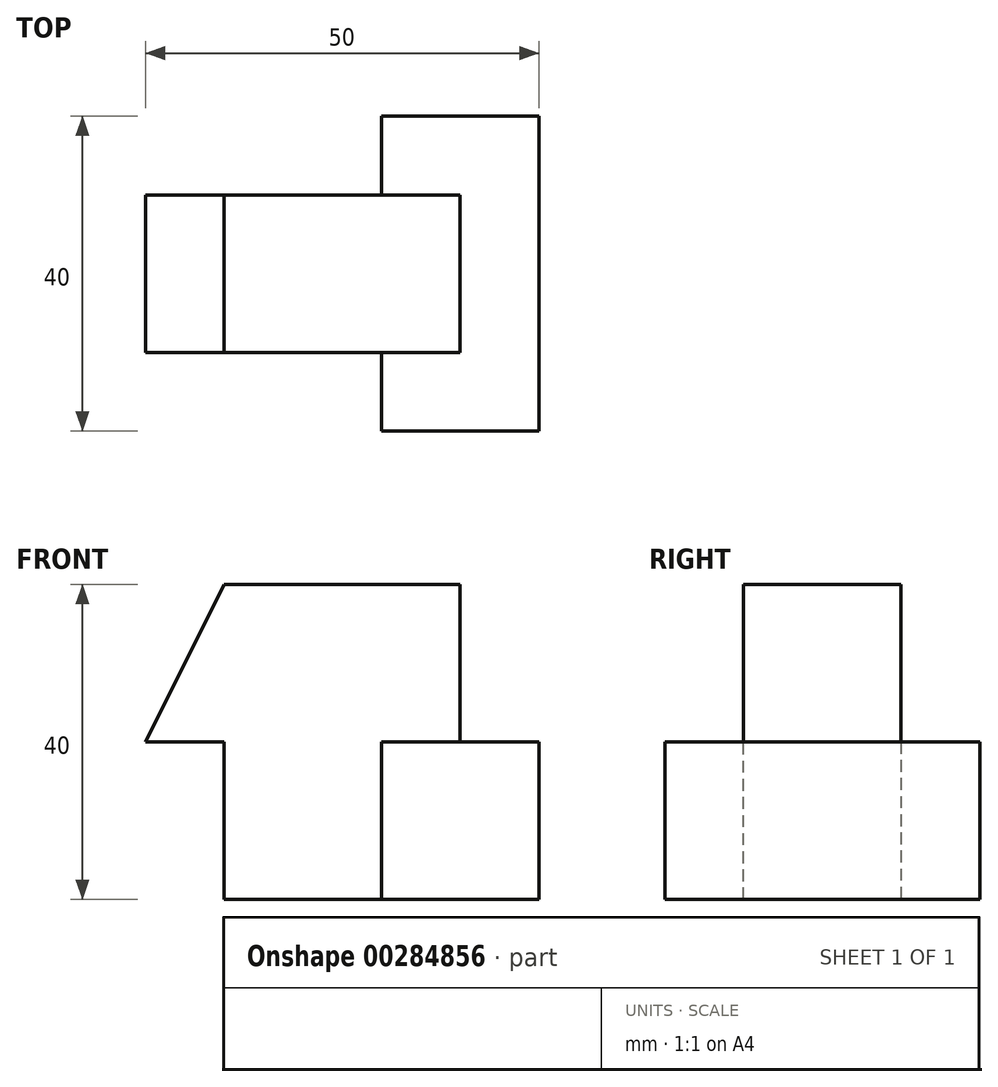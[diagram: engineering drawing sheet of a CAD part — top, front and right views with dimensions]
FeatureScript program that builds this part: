
annotation { "Feature Type Name" : "Feature", "Feature Type Description" : "" }
export const myFeature = defineFeature(function(context is Context, id is Id, definition is map)
    precondition{}
    {
        {
            var Q0;
            Q0=qCreatedBy(makeId("Front.planeOp"),FACE);
            var sketch = newSketch(context, id + "F0", { "sketchPlane" : qUnion([Q0])});
            skLineSegment(sketch, "E0.bottom", {"start": v(0, 0) * mm, "end": v(50, 0) * mm});
            skLineSegment(sketch, "E0.top", {"start": v(0, 40) * mm, "end": v(50, 40) * mm});
            skLineSegment(sketch, "E0.left", {"start": v(0, 0) * mm, "end": v(0, 40) * mm});
            skLineSegment(sketch, "E0.right", {"start": v(50, 0) * mm, "end": v(50, 40) * mm});
            skSolve(sketch);
        }
        {
            var Q0;
            Q0=makeQuery(id+"F0.imprint","IMPRINT",FACE,{"disambiguationData":[TD([[makeQuery(id+"F0.imprint","IMPRINT",EDGE,{"derivedFrom":sQuery(id+"F0.wireOp",EDGE,"E0.bottom")}),1.0]])]});
            extrude(context, id + "F1", {"entities" : qUnion([Q0]), "depth" : 40 * mm});
        }
        {
            var Q0;
            Q0=makeQuery(id+"F1.opExtrude","SWEPT_FACE",FACE,{"disambiguationData":[OSD([sQuery(id+"F0.wireOp",EDGE,"E0.left")])]});
            var sketch = newSketch(context, id + "F2", { "sketchPlane" : qUnion([Q0])});
            skLineSegment(sketch, "E1", {"start": v(0, 20) * mm, "end": v(40, 20) * mm});
            skLineSegment(sketch, "E2", {"start": v(30, 40) * mm, "end": v(30, 20) * mm});
            skLineSegment(sketch, "E3", {"start": v(10, 40) * mm, "end": v(10, 20) * mm});
            skLineSegment(sketch, "E4.0", {"start": v(40, 40) * mm, "end": v(0, 40) * mm});
            skLineSegment(sketch, "E5.0.1", {"start": v(40, 40) * mm, "end": v(40, 20) * mm});
            skLineSegment(sketch, "E5.0.3", {"start": v(40, 20) * mm, "end": v(40, 40) * mm});
            skLineSegment(sketch, "E6.0.1", {"start": v(0, 40) * mm, "end": v(0, 20) * mm});
            skLineSegment(sketch, "E6.0.3", {"start": v(0, 0) * mm, "end": v(0, 40) * mm});
            skPoint(sketch, "E7.orphan", {"position": v(40, 0) * mm});
            skPoint(sketch, "E8.orphan", {"position": v(0, 0) * mm});
            skSolve(sketch);
        }
        {
            var Q0;
            {var subQ3=sQuery(id+"F2.wireOp",EDGE,"E3");Q0=makeQuery(id+"F2.imprint","IMPRINT",FACE,{"disambiguationData":[TD([[makeQuery(id+"F2.imprint","IMPRINT",EDGE,{"derivedFrom":subQ3}),-1.0]])]});}
            var Q1;
            {var subQ2=sQuery(id+"F2.wireOp",EDGE,"E2");Q1=makeQuery(id+"F2.imprint","IMPRINT",FACE,{"disambiguationData":[TD([[makeQuery(id+"F2.imprint","IMPRINT",EDGE,{"derivedFrom":subQ2}),1.0]])]});}
            extrude(context, id + "F3", {"entities" : qUnion([Q0, Q1]), "operationType" : NewBodyOperationType.REMOVE, "endBound" : BoundingType.THROUGH_ALL, "oppositeDirection" : true, "depth" : 30 * mm});
        }
        {
            var Q0;
            {var subQ0=sQuery(id+"F2.wireOp",EDGE,"E1");Q0=makeQuery(id+"F3.boolean.opBoolean","COPY",FACE,{"derivedFrom":makeQuery(id+"F3.opExtrude","SWEPT_FACE",FACE,{"disambiguationData":[OSD([subQ0]),TDD([makeQuery(id+"F2.imprint","IMPRINT",EDGE,{"disambiguationData":[TD([[makeQuery(id+"F2.imprint","INTERSECT",VERTEX,{"derivedFrom":[subQ0,sQuery(id+"F2.wireOp",EDGE,"E6.0.3")]}),-1.0]])],"derivedFrom":subQ0})])]})});}
            var sketch = newSketch(context, id + "F4", { "sketchPlane" : qUnion([Q0])});
            skLineSegment(sketch, "E9.0", {"start": v(50, 0) * mm, "end": v(30, 0) * mm});
            skLineSegment(sketch, "E10.0", {"start": v(50, -10) * mm, "end": v(30, -10) * mm});
            skLineSegment(sketch, "E11.0", {"start": v(50, -30) * mm, "end": v(30, -30) * mm});
            skLineSegment(sketch, "E12.0", {"start": v(50, -40) * mm, "end": v(30, -40) * mm});
            skLineSegment(sketch, "E13", {"start": v(30, 0) * mm, "end": v(30, -10) * mm});
            skLineSegment(sketch, "E14", {"start": v(30, -30) * mm, "end": v(30, -40) * mm});
            skLineSegment(sketch, "E15.0", {"start": v(50, -30) * mm, "end": v(50, -40) * mm});
            skLineSegment(sketch, "E16.0", {"start": v(50, 0) * mm, "end": v(50, -10) * mm});
            skPoint(sketch, "E17.orphan", {"position": v(0, -10) * mm});
            skPoint(sketch, "E18.orphan", {"position": v(0, -30) * mm});
            skPoint(sketch, "E19.orphan", {"position": v(0, -40) * mm});
            skPoint(sketch, "E20.orphan", {"position": v(0, 0) * mm});
            skLineSegment(sketch, "E21.0", {"start": v(50, 0) * mm, "end": v(0, 0) * mm});
            skLineSegment(sketch, "E22.0", {"start": v(50, -10) * mm, "end": v(0, -10) * mm});
            skLineSegment(sketch, "E23.0", {"start": v(0, 0) * mm, "end": v(0, -10) * mm});
            skLineSegment(sketch, "E24.0", {"start": v(0, -30) * mm, "end": v(0, -40) * mm});
            skLineSegment(sketch, "E25.0", {"start": v(50, -40) * mm, "end": v(0, -40) * mm});
            skLineSegment(sketch, "E26.0", {"start": v(50, -30) * mm, "end": v(0, -30) * mm});
            skSolve(sketch);
        }
        {
            var Q0;
            {var subQ0=sQuery(id+"F4.wireOp",EDGE,"E13");Q0=makeQuery(id+"F4.imprint","IMPRINT",FACE,{"disambiguationData":[TD([[makeQuery(id+"F4.imprint","IMPRINT",EDGE,{"derivedFrom":subQ0}),-1.0]])]});}
            var Q1;
            {var subQ0=sQuery(id+"F4.wireOp",EDGE,"E14");Q1=makeQuery(id+"F4.imprint","IMPRINT",FACE,{"disambiguationData":[TD([[makeQuery(id+"F4.imprint","IMPRINT",EDGE,{"derivedFrom":subQ0}),-1.0]])]});}
            extrude(context, id + "F5", {"entities" : qUnion([Q0, Q1]), "operationType" : NewBodyOperationType.REMOVE, "endBound" : BoundingType.THROUGH_ALL, "oppositeDirection" : true, "depth" : 25 * mm});
        }
        {
            var Q0;
            Q0=makeQuery(id+"F1.opExtrude","SWEPT_FACE",FACE,{"disambiguationData":[OSD([sQuery(id+"F0.wireOp",EDGE,"E0.top")])]});
            var sketch = newSketch(context, id + "F6", { "sketchPlane" : qUnion([Q0])});
            skLineSegment(sketch, "E27", {"start": v(40, -10) * mm, "end": v(40, -30) * mm});
            skLineSegment(sketch, "E28.0", {"start": v(50, -10) * mm, "end": v(0, -10) * mm});
            skLineSegment(sketch, "E29.0", {"start": v(50, -30) * mm, "end": v(50, -10) * mm});
            skLineSegment(sketch, "E30.0", {"start": v(50, -30) * mm, "end": v(0, -30) * mm});
            skSolve(sketch);
        }
        {
            var Q0;
            Q0=qSketchRegion(id+"F6",true);
            var Q1;
            {var subQ0=sQuery(id+"F2.wireOp",EDGE,"E1");Q1=makeQuery(id+"F3.boolean.opBoolean","COPY",FACE,{"derivedFrom":makeQuery(id+"F3.opExtrude","SWEPT_FACE",FACE,{"disambiguationData":[OSD([subQ0]),TDD([makeQuery(id+"F2.imprint","IMPRINT",EDGE,{"disambiguationData":[TD([[makeQuery(id+"F2.imprint","INTERSECT",VERTEX,{"derivedFrom":[subQ0,sQuery(id+"F2.wireOp",EDGE,"E6.0.3")]}),-1.0]])],"derivedFrom":subQ0})])]})});}
            extrude(context, id + "F7", {"entities" : qUnion([Q0]), "operationType" : NewBodyOperationType.REMOVE, "endBound" : BoundingType.UP_TO_SURFACE, "oppositeDirection" : true, "endBoundEntityFace" : qUnion([Q1]), "depth" : 25 * mm});
        }
        {
            var Q0;
            Q0=makeQuery(id+"F5.boolean.opBoolean","MERGE",FACE,{"derivedFrom":[makeQuery(id+"F3.boolean.opBoolean","COPY",FACE,{"derivedFrom":makeQuery(id+"F3.opExtrude","SWEPT_FACE",FACE,{"disambiguationData":[OSD([sQuery(id+"F2.wireOp",EDGE,"E2")])]})}),makeQuery(id+"F5.opExtrude","SWEPT_FACE",FACE,{"disambiguationData":[OSD([sQuery(id+"F4.wireOp",EDGE,"E26.0")])]})]});
            var sketch = newSketch(context, id + "F8", { "sketchPlane" : qUnion([Q0])});
            skLineSegment(sketch, "E31.bottom", {"start": v(0, 40) * mm, "end": v(10, 40) * mm});
            skLineSegment(sketch, "E31.top", {"start": v(0, 20) * mm, "end": v(10, 20) * mm});
            skLineSegment(sketch, "E31.left", {"start": v(0, 40) * mm, "end": v(0, 20) * mm});
            skLineSegment(sketch, "E31.right", {"start": v(10, 40) * mm, "end": v(10, 20) * mm});
            skLineSegment(sketch, "E32", {"start": v(10, 40) * mm, "end": v(0, 20) * mm});
            skSolve(sketch);
        }
        {
            var Q0;
            Q0=makeQuery(id+"F8.imprint","IMPRINT",FACE,{"disambiguationData":[TD([[makeQuery(id+"F8.imprint","IMPRINT",EDGE,{"derivedFrom":sQuery(id+"F8.wireOp",EDGE,"E31.bottom")}),1.0]])]});
            extrude(context, id + "F9", {"entities" : qUnion([Q0]), "operationType" : NewBodyOperationType.REMOVE, "endBound" : BoundingType.THROUGH_ALL, "oppositeDirection" : true, "depth" : 25 * mm});
        }
        {
            var Q0;
            Q0=makeQuery(id+"F5.boolean.opBoolean","MERGE",FACE,{"derivedFrom":[makeQuery(id+"F3.boolean.opBoolean","COPY",FACE,{"derivedFrom":makeQuery(id+"F3.opExtrude","SWEPT_FACE",FACE,{"disambiguationData":[OSD([sQuery(id+"F2.wireOp",EDGE,"E2")])]})}),makeQuery(id+"F5.opExtrude","SWEPT_FACE",FACE,{"disambiguationData":[OSD([sQuery(id+"F4.wireOp",EDGE,"E26.0")])]})]});
            var sketch = newSketch(context, id + "F10", { "sketchPlane" : qUnion([Q0])});
            skLineSegment(sketch, "E33.bottom", {"start": v(0, 0) * mm, "end": v(10, 0) * mm});
            skLineSegment(sketch, "E33.top", {"start": v(0, 20) * mm, "end": v(10, 20) * mm});
            skLineSegment(sketch, "E33.left", {"start": v(0, 0) * mm, "end": v(0, 20) * mm});
            skLineSegment(sketch, "E33.right", {"start": v(10, 0) * mm, "end": v(10, 20) * mm});
            skSolve(sketch);
        }
        {
            var Q0;
            Q0 = qSketchRegion(id + "F10", true);
            extrude(context, id + "F11", {"entities" : qUnion([Q0]), "operationType" : NewBodyOperationType.REMOVE, "endBound" : BoundingType.THROUGH_ALL, "oppositeDirection" : true, "depth" : 25 * mm});
        }
    });
